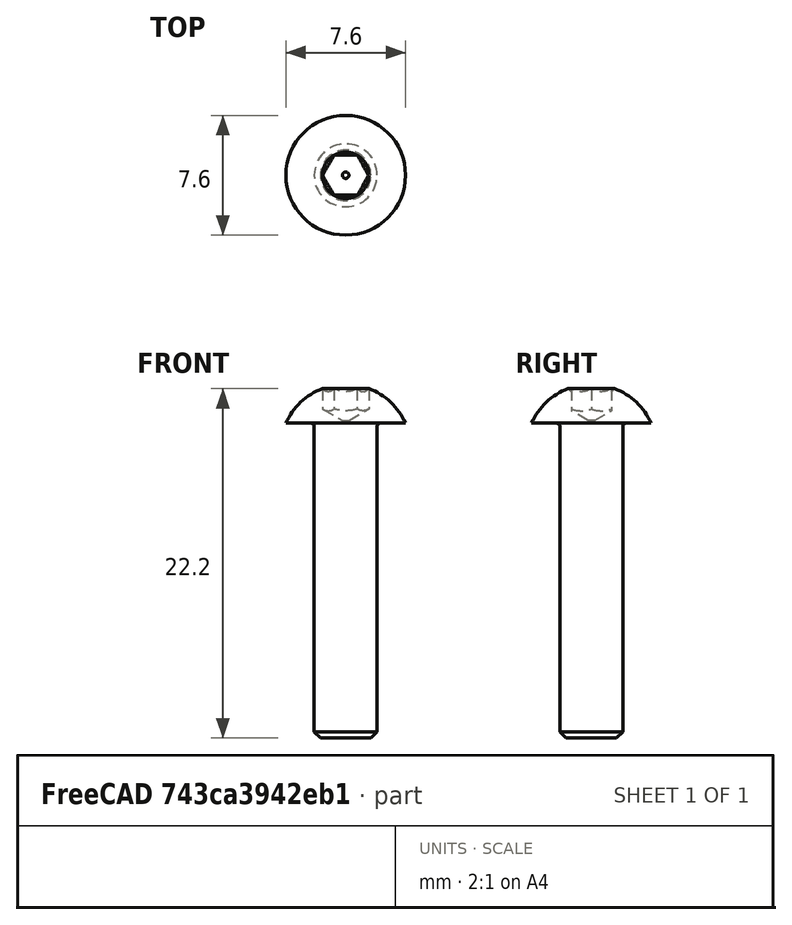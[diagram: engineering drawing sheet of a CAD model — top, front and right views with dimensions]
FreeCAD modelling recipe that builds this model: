
FCSTD DOCUMENT  (FreeCAD 0.20R29603 (Git))
Label: Assembly4_multifile_test
License: All rights reserved
LicenseURL: http://en.wikipedia.org/wiki/All_rights_reserved
objects: App::DocumentObjectGroup×3, PartDesign::CoordinateSystem×1, App::FeaturePython×1, App::Link×1, Part::FeaturePython×1, App::Part×1
note: 2 computed .brp shape members not serialized (recipe doc carries the construction recipe); baked Part::Feature solids carry a one-line shape summary decoded from their .brp
EXTERNAL_REF file=block.FCStd obj=Local_CS
EXTERNAL_REF file=block.FCStd obj=Body
EXTERNAL_REF file=block.FCStd obj=HoleAxis_1

FEATURE [App::DocumentObjectGroup] Parts
FEATURE [PartDesign::CoordinateSystem] LCS_Origin
  AttacherType = Attacher::AttachEngine3D
  MapMode = 2
  Support = -> [X_Axis]
FEATURE [App::DocumentObjectGroup] Constraints
FEATURE [App::FeaturePython] Variables  # WARN: FeaturePython — macro-defined, semantics opaque (R4)
  Type = App::PropertyContainer
FEATURE [App::DocumentObjectGroup] Configurations
FEATURE [App::Link] block
  AssemblyType = Part::Link
  AttachedBy = #Local_CS
  AttachedTo = Parent Assembly#LCS_Origin
  LinkedObject = -> <external block.FCStd>#Body
  SolverId = Asm4EE
  expr: Placement = LCS_Origin.Placement * AttachmentOffset * block#Local_CS.Placement ^ -1
FEATURE [Part::FeaturePython] Screw  label="M4x20-Screw"  # Fasteners workbench fastener (typed FeaturePython)
  AssemblyType = Part::Link
  AttachedBy = Origin
  AttachedTo = block#HoleAxis_1
  Placement = pos=(0,0,20) rot=(0,0,1;0rad)
  SolverId = Asm4EE
  diameter = 2
  invert = false
  leftHanded = false
  length = 6
  lengthCustom = 20
  matchOuter = false
  offset = 0
  thread = false
  type = 51
  expr: Placement = block.Placement * block#HoleAxis_1.Placement * AttachmentOffset
FEATURE [App::Part] Model
  AssemblyType = Part::Link
  Group = -> [LCS_Origin,Constraints,Variables,Configurations,block,Screw]
  Origin = -> Origin
  Type = Assembly

RESOLVED EXTERNAL PARTS (link-assembly join: the EXTERNAL_REF files above that resolve inside this repo's crawl, each included once):
---- part block.FCStd = doc fcstd_cc372cc186db ----
FCSTD DOCUMENT  (FreeCAD 0.20R29603 (Git))
Label: block
License: All rights reserved
LicenseURL: http://en.wikipedia.org/wiki/All_rights_reserved
objects: Sketcher::SketchObject×4, PartDesign::Plane×2, PartDesign::Pad×1, PartDesign::Pocket×1, PartDesign::SubtractivePipe×1, PartDesign::CoordinateSystem×1, PartDesign::Line×1, PartDesign::Body×1
note: 15 computed .brp shape members not serialized (recipe doc carries the construction recipe); baked Part::Feature solids carry a one-line shape summary decoded from their .brp

FEATURE [Sketcher::SketchObject] Sketch
  FullyConstrained = true
  MapMode = 5
  Support = -> [XY_Plane]
  sketch-geometry (4):
    g0: LineSegment StartX=-10 StartY=-10 StartZ=0 EndX=10 EndY=-10 EndZ=0
    g1: LineSegment StartX=10 StartY=-10 StartZ=0 EndX=10 EndY=10 EndZ=0
    g2: LineSegment StartX=10 StartY=10 StartZ=0 EndX=-10 EndY=10 EndZ=0
    g3: LineSegment StartX=-10 StartY=10 StartZ=0 EndX=-10 EndY=-10 EndZ=0
  constraints (11):
    c: Coincident(g0,g1)
    c: Coincident(g1,g2)
    c: Coincident(g2,g3)
    c: Coincident(g3,g0)
    c: Horizontal(g0)
    c: Horizontal(g2)
    c: Vertical(g1)
    c: Vertical(g3)
    c: Symmetric(g1,g0,g-1)
    c: Equal(g2,g3)
    c: Distance(g2) = 20
FEATURE [PartDesign::Pad] Pad
  Direction = (0,0,1)
  Length = 20
  Length2 = 10
  Profile = -> Sketch
  ReferenceAxis = -> Sketch [N_Axis]
  Type = 0
FEATURE [PartDesign::Plane] DatumPlane  label="topPlane"
  AttachmentOffset = pos=(0,0,20) rot=(0,0,1;0rad)
  Length = 60
  MapMode = 5
  Placement = pos=(0,0,20) rot=(0,0,1;0rad)
  ResizeMode = 0
  Support = -> [XY_Plane]
  Width = 60
FEATURE [Sketcher::SketchObject] Sketch001
  FullyConstrained = true
  MapMode = 5
  Placement = pos=(0,0,20) rot=(0,0,1;0rad)
  Support = -> [DatumPlane]
  sketch-geometry (1):
    g0: Circle CenterX=0 CenterY=0 CenterZ=0 NormalX=0 NormalY=0 NormalZ=1 AngleXU=0 Radius=2
  constraints (2):
    c: Coincident(g0,g-1)
    c: Diameter(g0) = 4
FEATURE [PartDesign::Pocket] Pocket
  BaseFeature = -> Pad
  Direction = (0,0,-1)
  Length = 20
  Length2 = 5
  Profile = -> Sketch001
  ReferenceAxis = -> Sketch001 [N_Axis]
  Type = 0
FEATURE [PartDesign::Plane] DatumPlane001  label="Crossplane"
  Length = 60
  MapMode = 5
  Placement = pos=(0,0,0) rot=(1,0,0;1.5708rad)
  ResizeMode = 0
  Support = -> [XZ_Plane]
  Width = 60
FEATURE [Sketcher::SketchObject] Sketch002  label="topFilletProfile"
  FullyConstrained = true
  MapMode = 5
  Placement = pos=(0,0,0) rot=(1,0,0;1.5708rad)
  Support = -> [DatumPlane001]
  sketch-geometry (9):
    g0: LineSegment StartX=0 StartY=0 StartZ=0 EndX=10 EndY=0 EndZ=0
    g1: LineSegment StartX=10 StartY=0 StartZ=0 EndX=10 EndY=20 EndZ=0
    g2: LineSegment StartX=10 StartY=20 StartZ=0 EndX=0 EndY=20 EndZ=0
    g3: LineSegment StartX=0 StartY=20 StartZ=0 EndX=0 EndY=0 EndZ=0
    g4: LineSegment StartX=7 StartY=20 StartZ=0 EndX=10 EndY=20 EndZ=0
    g5: LineSegment StartX=10 StartY=20 StartZ=0 EndX=10 EndY=17 EndZ=0
    g6: ArcOfCircle CenterX=7 CenterY=17 CenterZ=0 NormalX=0 NormalY=0 NormalZ=1 AngleXU=0 Radius=3 StartAngle=-9e-16 EndAngle=1.5708
    g7: LineSegment StartX=7 StartY=20 StartZ=0 EndX=7 EndY=17 EndZ=0
    g8: LineSegment StartX=7 StartY=17 StartZ=0 EndX=10 EndY=17 EndZ=0
  constraints (24):
    c: Coincident(g0,g1)
    c: Coincident(g1,g2)
    c: Coincident(g2,g3)
    c: Coincident(g3,g0)
    c: Horizontal(g0)
    c: Horizontal(g2)
    c: Vertical(g1)
    c: Vertical(g3)
    c: Coincident(g0,g-1)
    c: Distance(g1) = 20
    c: Distance(g2) = 10
    c: Horizontal(g4)
    c: Coincident(g4,g5)
    c: Vertical(g5)
    c: Coincident(g4,g1)
    c: Equal(g5,g4)
    c: Distance(g4) = 3
    c: Coincident(g6,g4)
    c: Coincident(g6,g5)
    c: Coincident(g4,g7)
    c: Vertical(g7)
    c: Coincident(g7,g8)
    c: Coincident(g8,g5)
    c: Coincident(g6,g7)
FEATURE [Sketcher::SketchObject] Sketch003  label="topFilletPath"
  FullyConstrained = true
  MapMode = 5
  Placement = pos=(0,0,20) rot=(0,0,1;0rad)
  Support = -> [DatumPlane]
  sketch-geometry (4):
    g0: LineSegment StartX=-10 StartY=-10 StartZ=0 EndX=10 EndY=-10 EndZ=0
    g1: LineSegment StartX=10 StartY=-10 StartZ=0 EndX=10 EndY=10 EndZ=0
    g2: LineSegment StartX=10 StartY=10 StartZ=0 EndX=-10 EndY=10 EndZ=0
    g3: LineSegment StartX=-10 StartY=10 StartZ=0 EndX=-10 EndY=-10 EndZ=0
  constraints (11):
    c: Coincident(g0,g1)
    c: Coincident(g1,g2)
    c: Coincident(g2,g3)
    c: Coincident(g3,g0)
    c: Horizontal(g0)
    c: Horizontal(g2)
    c: Vertical(g1)
    c: Vertical(g3)
    c: Symmetric(g1,g0,g-1)
    c: Equal(g1,g2)
    c: Distance(g2) = 20
FEATURE [PartDesign::SubtractivePipe] SubtractivePipe  label="top fillet"
  AuxilleryCurvelinear = true
  AuxillerySpineTangent = false
  BaseFeature = -> Pocket
  Binormal = (0,0,0)
  Mode = 0
  Profile = -> Sketch002
  Spine = -> Sketch003
  SpineTangent = false
  Transformation = 0
  Transition = 2
FEATURE [PartDesign::CoordinateSystem] Local_CS
  AttacherType = Attacher::AttachEngine3D
  MapMode = 1
FEATURE [PartDesign::Line] HoleAxis_1
  AttacherType = Attacher::AttachEngineLine
  Length = 5.63627
  MapMode = 19
  Placement = pos=(0,0,20) rot=(0,0,1;0rad)
  ResizeMode = 1
  Support = -> [SubtractivePipe]
FEATURE [PartDesign::Body] Body  label="block"
  Group = -> [Sketch,Pad,DatumPlane,Sketch001,Pocket,DatumPlane001,Sketch002,Sketch003,SubtractivePipe,Local_CS,HoleAxis_1]
  Origin = -> Origin
  Tip = -> SubtractivePipe
